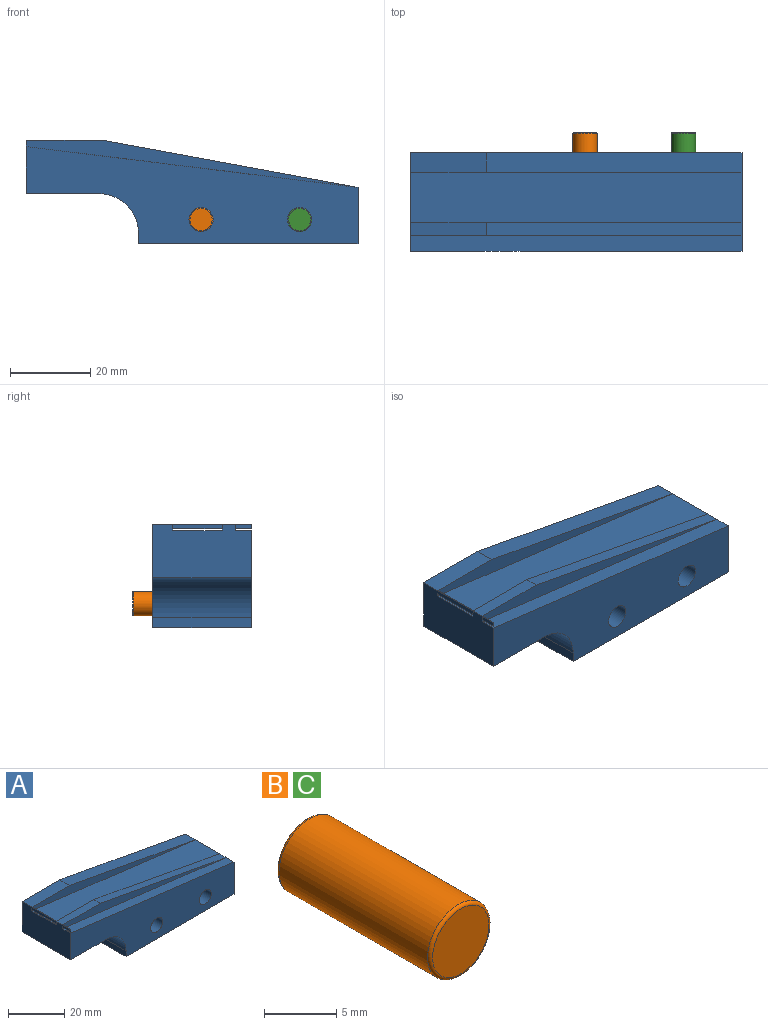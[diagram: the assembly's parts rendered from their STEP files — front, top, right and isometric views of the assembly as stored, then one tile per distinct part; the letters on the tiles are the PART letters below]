
ASSEMBLY  parts=3 mates=2
PART A: 25 faces, bbox 82.5x24.5x25.8 mm
  f0: plane 82.5x11.73mm, normal (0,-1,0), area 177.2mm2, adj f7,f8,f13,f14,f24
  f1: plane 24.5x14.02mm, normal (1,0,0), area 343.5mm2, adj f2,f6,f12,f14,f16,f23,f24
  f2: plane 82.5x25.75mm, normal (0,1,0), area 1298.5mm2, adj f1,f7,f8,f9,f10,f11,f12,f17
  f3: plane 82.5x11.73mm, normal (0,1,0), area 177.2mm2, adj f7,f8,f15,f16,f24
  f4: plane 82.5x11.73mm, normal (0,-1,0), area 177.2mm2, adj f7,f8,f15,f16,f23
  f5: plane 1.11x0.14mm, normal (0,-1,0), area 0.1mm2, adj f7,f8,f13
  f6: plane 82.5x24.15mm, normal (0,-1,0), area 1189.6mm2, adj f1,f8,f9,f10,f11,f12,f14,f17
  f7: plane 24.5x19mm, normal (0,0,1), area 158mm2, adj f0,f2,f3,f4,f5,f8,f13,f15
  f8: plane 24.5x13.25mm, normal (-1,0,0), area 316.7mm2, adj f0,f2,f3,f4,f5,f6,f7,f9
  f9: plane 24.5x18mm, normal (0,0,-1), area 441mm2, adj f2,f6,f8,f10
  f10: cylinder r=10mm len=24.5mm, axis (0,1,0), area 384.8mm2, adj f2,f6,f9,f11
  f11: plane 24.5x2.5mm, normal (-1,0,0), area 61.2mm2, adj f2,f6,f10,f12
  f12: plane 54.5x24.5mm, normal (0,0,-1), area 1335.2mm2, adj f1,f2,f6,f11
  f13: plane 4x1.11mm, normal (0.99,0,-0.12), area 4.5mm2, adj f0,f5,f7,f8
  f14: plane 82.5x10.13mm, normal (0.12,0,0.99), area 332.5mm2, adj f0,f1,f6,f8
  f15: plane 12.3x1.11mm, normal (0.99,0,-0.12), area 13.8mm2, adj f3,f4,f7,f8
  f16: plane 82.5x12.3mm, normal (0.12,0,0.99), area 1022.4mm2, adj f1,f3,f4,f8
  f17: cylinder r=3mm len=24.5mm, axis (0,1,0), area 461.8mm2, adj f2,f6
  f18: cylinder r=3mm len=24.5mm, axis (0,1,0), area 461.8mm2, adj f2,f6
  f19: cone r=0mm half-angle=59deg, axis (0,1,0), area 39.9mm2, adj f20
  f20: cylinder r=3.3mm len=18mm, axis (0,1,0), area 373.2mm2, adj f2,f19
  f21: cone r=0mm half-angle=59deg, axis (0,1,0), area 39.9mm2, adj f22
  f22: cylinder r=3.3mm len=18mm, axis (0,1,0), area 373.2mm2, adj f2,f21
  f23: plane 63.5x11.73mm, normal (0.18,0,0.98), area 319.6mm2, adj f1,f2,f4,f7
  f24: plane 63.5x11.73mm, normal (0.18,0,0.98), area 209.9mm2, adj f0,f1,f3,f7
PART B: 5 faces, bbox 6.5x15x6.5 mm
  f0: cylinder r=3mm len=14.5mm, axis (0,1,0), area 273.3mm2, adj f3,f4
  f1: plane 5.5x5.5mm, normal (0,-1,0), area 23.8mm2, adj f4
  f2: plane 5.5x5.5mm, normal (0,1,0), area 23.8mm2, adj f3
  f3: torus R=2.75mm, axis (0,-1,0), area 7.2mm2, adj f0,f2
  f4: torus R=2.75mm, axis (0,-1,0), area 7.2mm2, adj f0,f1
PART C: same geometry as B
PLACE A t=(-5.62,-5.08,1.71)mm
PLACE B rot(axis=(1,0,0),180deg) t=(-44.62,-15.08,7.71)mm
PLACE C rot(axis=(1,0,0),180deg) t=(-20.12,-15.08,7.71)mm
MATE fastened C.f0 <-> A.f17  axis (0,1,0) through (-20.12,-0.08,7.71)mm
MATE fastened B.f0 <-> A.f18  axis (0,1,0) through (-44.62,-0.08,7.71)mm
